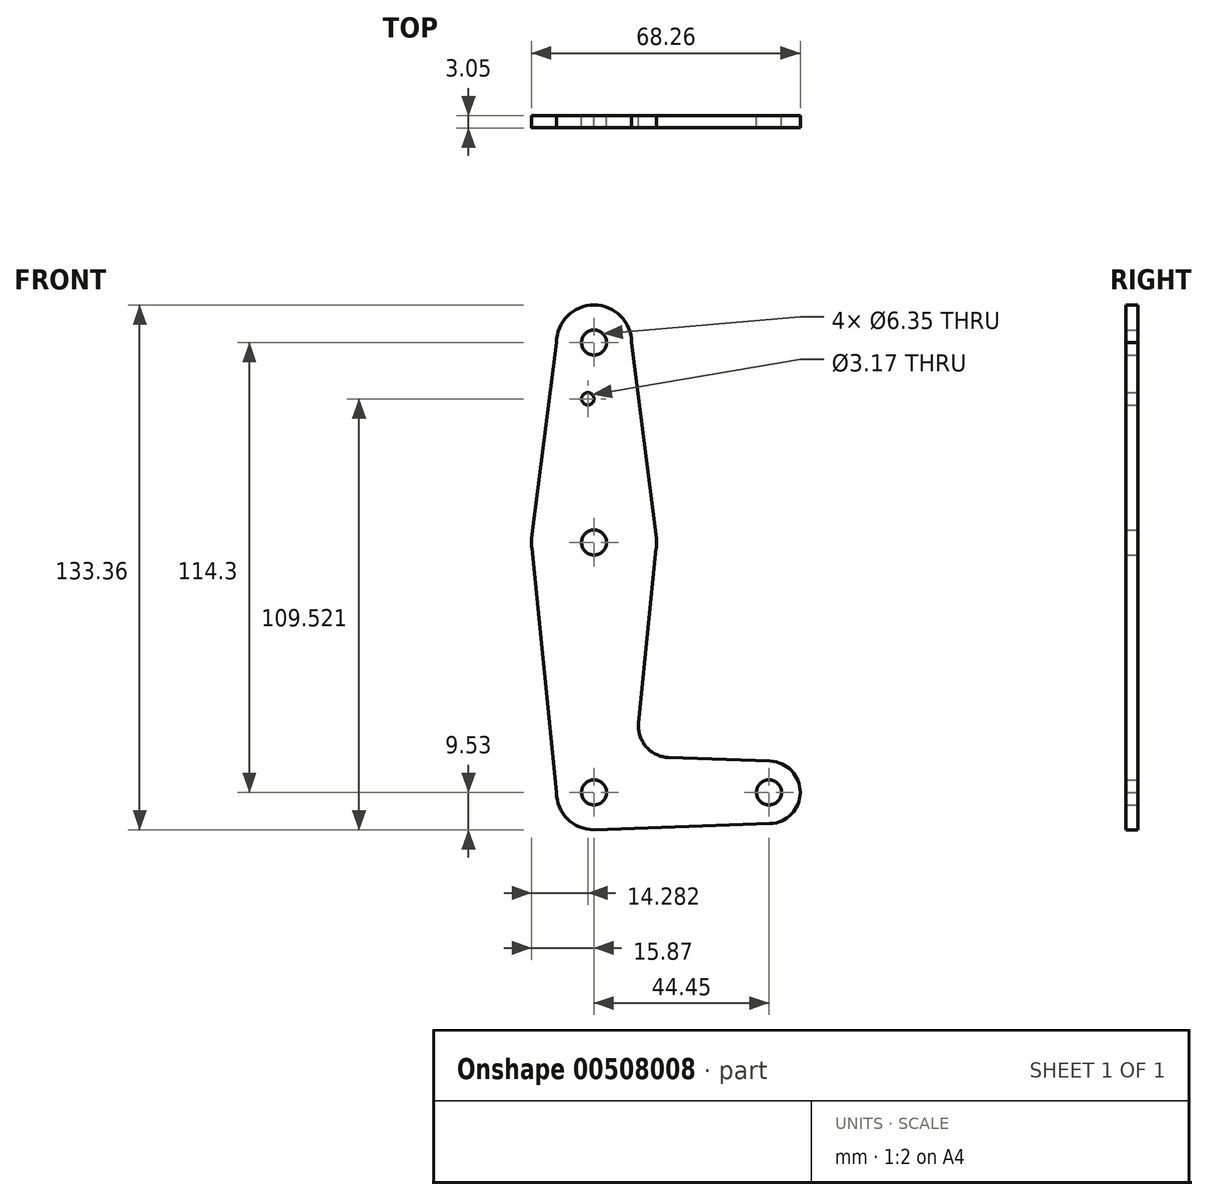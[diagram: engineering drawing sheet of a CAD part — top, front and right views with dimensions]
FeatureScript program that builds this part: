
annotation { "Feature Type Name" : "Feature", "Feature Type Description" : "" }
export const myFeature = defineFeature(function(context is Context, id is Id, definition is map)
    precondition{}
    {
        {
            var Q0;
            Q0=qCreatedBy(makeId("Front.planeOp"),FACE);
            var sketch = newSketch(context, id + "F0", { "sketchPlane" : qUnion([Q0])});
            skLineSegment(sketch, "E0", {"start": v(0, 0) * mm, "end": v(0, 114.3) * mm});
            skLineSegment(sketch, "E1", {"start": v(0, 0) * mm, "end": v(44.45, 0) * mm});
            skCircle(sketch, "E2", {"center": v(0, 0) * mm, "radius": 9.53 * mm});
            skCircle(sketch, "E3", {"center": v(44.45, 0) * mm, "radius": 7.94 * mm});
            skCircle(sketch, "E4", {"center": v(0, 114.3) * mm, "radius": 9.53 * mm});
            skCircle(sketch, "E5", {"center": v(0, 63.5) * mm, "radius": 15.88 * mm});
            skLineSegment(sketch, "E6", {"start": v(0, -9.53) * mm, "end": v(44.73, -7.93) * mm});
            skLineSegment(sketch, "E7", {"start": v(18.97, 8.85) * mm, "end": v(44.73, 7.93) * mm});
            skLineSegment(sketch, "E8", {"start": v(-9.52, 114.3) * mm, "end": v(-15.75, 65.5) * mm});
            skLineSegment(sketch, "E9", {"start": v(15.75, 65.5) * mm, "end": v(9.52, 114.3) * mm});
            skLineSegment(sketch, "E10", {"start": v(15.8, 61.91) * mm, "end": v(11.34, 17.59) * mm});
            skLineSegment(sketch, "E11", {"start": v(-15.8, 61.9) * mm, "end": v(-9.52, 0) * mm});
            skCircle(sketch, "E12", {"center": v(0, 114.3) * mm, "radius": 3.18 * mm});
            skCircle(sketch, "E13", {"center": v(0, 63.5) * mm, "radius": 3.18 * mm});
            skCircle(sketch, "E14", {"center": v(0, 0) * mm, "radius": 3.18 * mm});
            skCircle(sketch, "E15", {"center": v(44.45, 0) * mm, "radius": 3.18 * mm});
            skCircle(sketch, "E16", {"center": v(-1.59, 100) * mm, "radius": 1.59 * mm});
            skArc(sketch, "E17.filletArc", {"start": v(11.34, 17.59) * mm, "mid": v(13.26, 11.57) * mm, "end": v(18.97, 8.85) * mm});
            skSolve(sketch);
        }
        {
            var Q0;
            {var subQ0=sQuery(id+"F0.wireOp",EDGE,"E8");Q0=makeQuery(id+"F0.imprint","IMPRINT",FACE,{"disambiguationData":[TD([[makeQuery(id+"F0.imprint","IMPRINT",EDGE,{"derivedFrom":subQ0}),1.0]])]});}
            var Q1;
            {var subQ0=sQuery(id+"F0.wireOp",EDGE,"E9");Q1=makeQuery(id+"F0.imprint","IMPRINT",FACE,{"disambiguationData":[TD([[makeQuery(id+"F0.imprint","IMPRINT",EDGE,{"derivedFrom":subQ0}),1.0]])]});}
            var Q2;
            Q2=makeQuery(id+"F0.imprint","IMPRINT",FACE,{"disambiguationData":[TD([[makeQuery(id+"F0.imprint","IMPRINT",EDGE,{"derivedFrom":sQuery(id+"F0.wireOp",EDGE,"E12")}),-1.0]])]});
            var Q3;
            {var subQ0=sQuery(id+"F0.wireOp",EDGE,"E5");var subQ4=sQuery(id+"F0.wireOp",EDGE,"E0");var subQ7=makeQuery(id+"F0.imprint","INTERSECT",VERTEX,{"disambiguationData":[OD(0.0)],"derivedFrom":[subQ4,subQ0]});Q3=makeQuery(id+"F0.imprint","IMPRINT",FACE,{"disambiguationData":[TD([[makeQuery(id+"F0.imprint","IMPRINT",EDGE,{"disambiguationData":[TD([[subQ7,-1.0]])],"derivedFrom":subQ4}),1.0]])]});}
            var Q4;
            {var subQ0=sQuery(id+"F0.wireOp",EDGE,"E5");var subQ2=sQuery(id+"F0.wireOp",EDGE,"E0");var subQ3=makeQuery(id+"F0.imprint","INTERSECT",VERTEX,{"disambiguationData":[OD(0.0)],"derivedFrom":[subQ2,subQ0]});Q4=makeQuery(id+"F0.imprint","IMPRINT",FACE,{"disambiguationData":[TD([[makeQuery(id+"F0.imprint","IMPRINT",EDGE,{"disambiguationData":[TD([[subQ3,-1.0]])],"derivedFrom":subQ2}),-1.0]])]});}
            var Q5;
            {var subQ5=sQuery(id+"F0.wireOp",EDGE,"E11");Q5=makeQuery(id+"F0.imprint","IMPRINT",FACE,{"disambiguationData":[TD([[makeQuery(id+"F0.imprint","IMPRINT",EDGE,{"derivedFrom":subQ5}),1.0]])]});}
            var Q6;
            {var subQ0=sQuery(id+"F0.wireOp",EDGE,"E7");Q6=makeQuery(id+"F0.imprint","IMPRINT",FACE,{"disambiguationData":[TD([[makeQuery(id+"F0.imprint","IMPRINT",EDGE,{"derivedFrom":subQ0}),-1.0]])]});}
            var Q7;
            {var subQ0=sQuery(id+"F0.wireOp",EDGE,"E3");var subQ1=sQuery(id+"F0.wireOp",EDGE,"E1");var subQ2=makeQuery(id+"F0.imprint","INTERSECT",VERTEX,{"derivedFrom":[subQ1,subQ0]});Q7=makeQuery(id+"F0.imprint","IMPRINT",FACE,{"disambiguationData":[TD([[makeQuery(id+"F0.imprint","IMPRINT",EDGE,{"disambiguationData":[TD([[subQ2,1.0]])],"derivedFrom":subQ1}),-1.0]])]});}
            var Q8;
            Q8=makeQuery(id+"F0.imprint","IMPRINT",FACE,{"disambiguationData":[TD([[makeQuery(id+"F0.imprint","IMPRINT",EDGE,{"derivedFrom":sQuery(id+"F0.wireOp",EDGE,"E15")}),-1.0]])]});
            var Q9;
            {var subQ4=sQuery(id+"F0.wireOp",EDGE,"E0");var subQ6=sQuery(id+"F0.wireOp",EDGE,"E14");var subQ7=makeQuery(id+"F0.imprint","INTERSECT",VERTEX,{"derivedFrom":[subQ4,subQ6]});Q9=makeQuery(id+"F0.imprint","IMPRINT",FACE,{"disambiguationData":[TD([[makeQuery(id+"F0.imprint","IMPRINT",EDGE,{"disambiguationData":[TD([[subQ7,-1.0]])],"derivedFrom":subQ4}),1.0]])]});}
            var Q10;
            {var subQ0=sQuery(id+"F0.wireOp",EDGE,"E14");var subQ1=sQuery(id+"F0.wireOp",EDGE,"E0");var subQ2=makeQuery(id+"F0.imprint","INTERSECT",VERTEX,{"derivedFrom":[subQ1,subQ0]});Q10=makeQuery(id+"F0.imprint","IMPRINT",FACE,{"disambiguationData":[TD([[makeQuery(id+"F0.imprint","IMPRINT",EDGE,{"disambiguationData":[TD([[subQ2,-1.0]])],"derivedFrom":subQ1}),-1.0]])]});}
            extrude(context, id + "F1", {"entities" : qUnion([Q0, Q1, Q2, Q3, Q4, Q5, Q6, Q7, Q8, Q9, Q10]), "depth" : 3.05 * mm});
        }
    });
